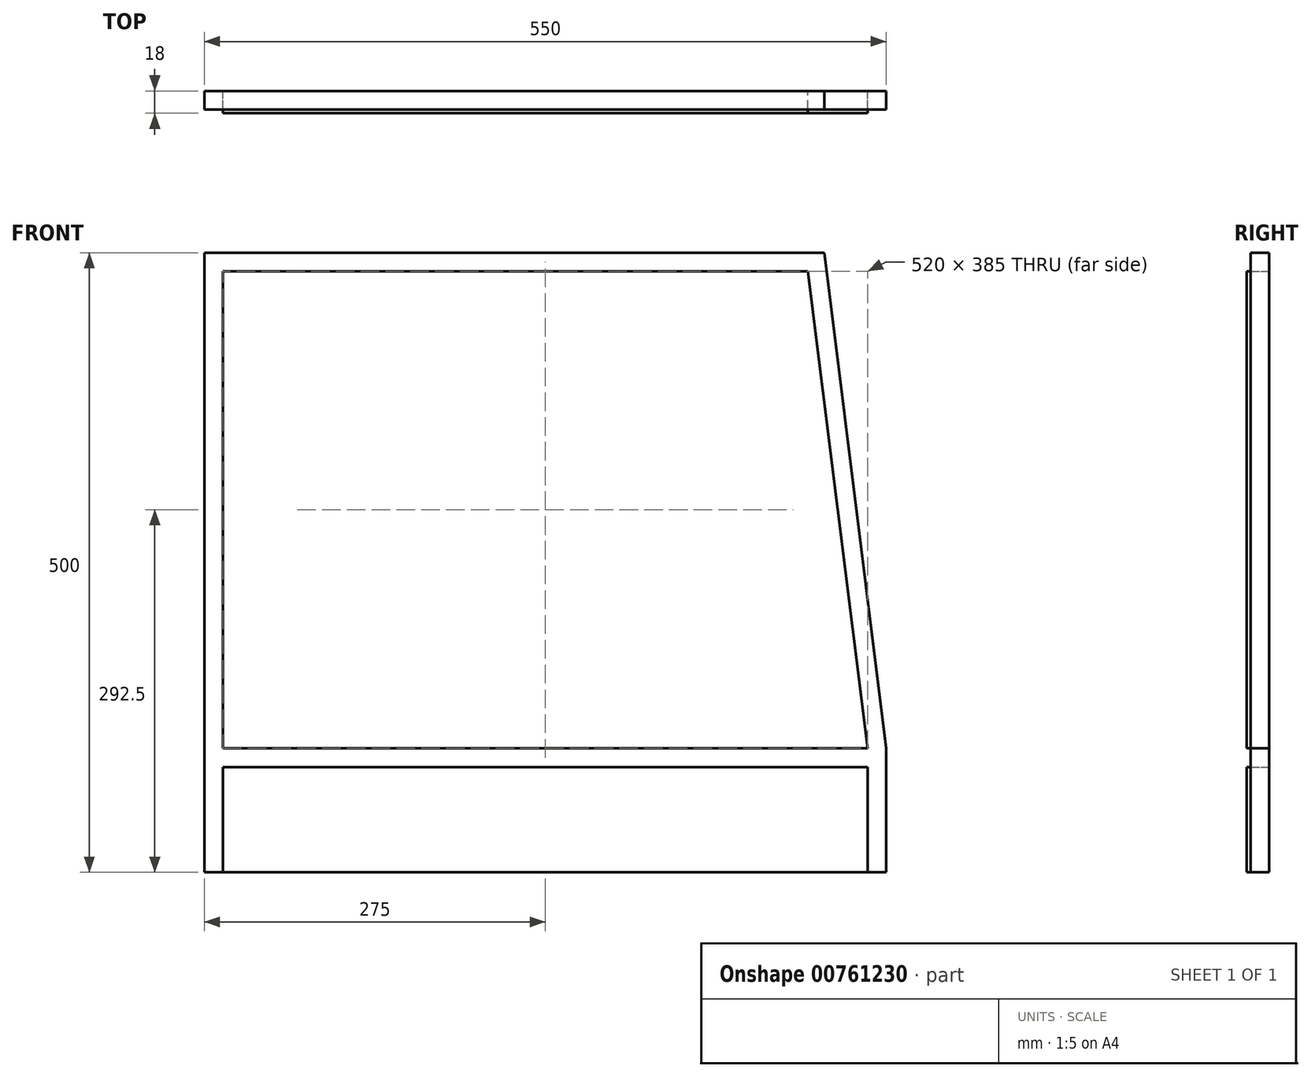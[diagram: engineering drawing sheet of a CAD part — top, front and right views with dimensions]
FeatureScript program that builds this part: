
annotation { "Feature Type Name" : "Feature", "Feature Type Description" : "" }
export const myFeature = defineFeature(function(context is Context, id is Id, definition is map)
    precondition{}
    {
        {
            var Q0;
            Q0=qCreatedBy(makeId("Front.planeOp"),FACE);
            var sketch = newSketch(context, id + "F0", { "sketchPlane" : qUnion([Q0])});
            skLineSegment(sketch, "E0.bottom", {"start": v(225, 250) * mm, "end": v(-275, 250) * mm});
            skLineSegment(sketch, "E0.top", {"start": v(275, -250) * mm, "end": v(-275, -250) * mm});
            skLineSegment(sketch, "E0.left", {"start": v(275, -150) * mm, "end": v(275, -250) * mm});
            skLineSegment(sketch, "E0.right", {"start": v(-275, 250) * mm, "end": v(-275, -250) * mm});
            skPoint(sketch, "E0.middle", {"position": v(0, 0) * mm});
            skLineSegment(sketch, "E1", {"start": v(275, -150) * mm, "end": v(225, 250) * mm});
            skPoint(sketch, "E2.orphan", {"position": v(275, 250) * mm});
            skLineSegment(sketch, "E3", {"start": v(260, -150) * mm, "end": v(-260, -150) * mm});
            skLineSegment(sketch, "E4", {"start": v(-260, -165) * mm, "end": v(260, -165) * mm});
            skLineSegment(sketch, "E5", {"start": v(-260, 235) * mm, "end": v(-260, -150) * mm});
            skLineSegment(sketch, "E6", {"start": v(260, -250) * mm, "end": v(260, -165) * mm});
            skLineSegment(sketch, "E7", {"start": v(260, -150) * mm, "end": v(211.87, 235) * mm});
            skLineSegment(sketch, "E8", {"start": v(-260, 235) * mm, "end": v(211.87, 235) * mm});
            skPoint(sketch, "E9.orphan", {"position": v(-275, 235) * mm});
            skPoint(sketch, "E10.orphan", {"position": v(-260, 250) * mm});
            skPoint(sketch, "E11.orphan", {"position": v(225, 235) * mm});
            skPoint(sketch, "E12.orphan", {"position": v(-275, -165) * mm});
            skPoint(sketch, "E13.orphan", {"position": v(-275, -150) * mm});
            skLineSegment(sketch, "E14.trimOffspring", {"start": v(-260, -165) * mm, "end": v(-260, -250) * mm});
            skSolve(sketch);
        }
        {
            var Q0;
            Q0=makeQuery(id+"F0.imprint","IMPRINT",FACE,{"disambiguationData":[TD([[makeQuery(id+"F0.imprint","IMPRINT",EDGE,{"derivedFrom":sQuery(id+"F0.wireOp",EDGE,"E3")}),-1.0]])]});
            var Q1;
            Q1=makeQuery(id+"F0.imprint","IMPRINT",FACE,{"disambiguationData":[TD([[makeQuery(id+"F0.imprint","IMPRINT",EDGE,{"derivedFrom":sQuery(id+"F0.wireOp",EDGE,"E4")}),-1.0]])]});
            extrude(context, id + "F1", {"entities" : qUnion([Q0, Q1]), "depth" : 18 * mm, "offsetDistance" : 25 * mm});
        }
        {
            var Q0;
            Q0=makeQuery(id+"F0.imprint","IMPRINT",FACE,{"disambiguationData":[TD([[makeQuery(id+"F0.imprint","IMPRINT",EDGE,{"derivedFrom":sQuery(id+"F0.wireOp",EDGE,"E0.bottom")}),1.0]])]});
            extrude(context, id + "F2", {"entities" : qUnion([Q0]), "depth" : 15 * mm, "offsetDistance" : 25 * mm});
        }
    });
